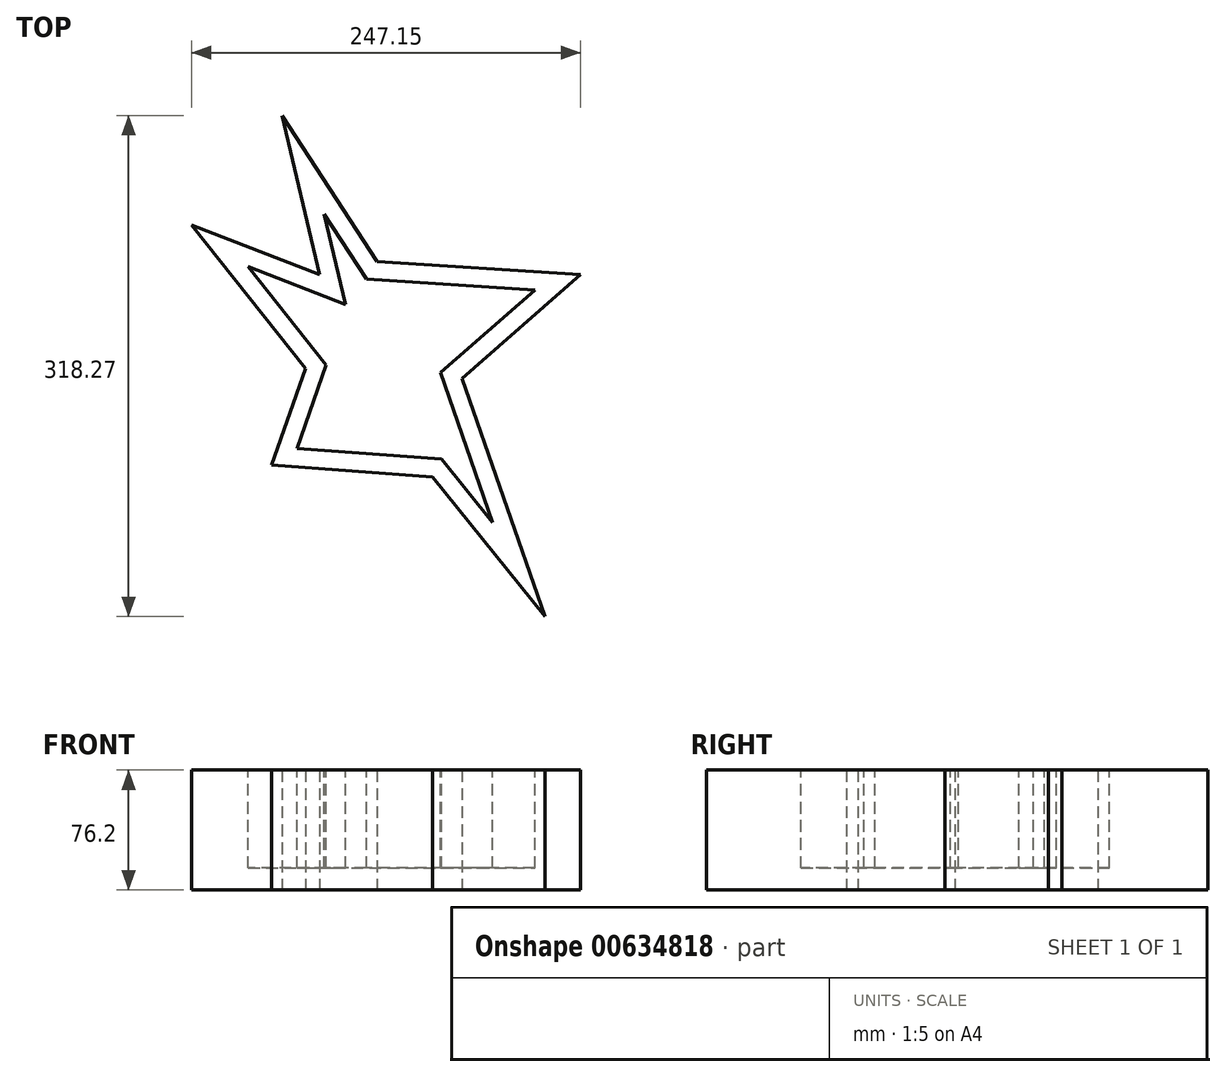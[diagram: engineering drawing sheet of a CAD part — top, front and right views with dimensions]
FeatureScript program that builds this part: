
annotation { "Feature Type Name" : "Feature", "Feature Type Description" : "" }
export const myFeature = defineFeature(function(context is Context, id is Id, definition is map)
    precondition{}
    {
        {
            var Q0;
            Q0=qCreatedBy(makeId("Top.planeOp"),FACE);
            var sketch = newSketch(context, id + "F0", { "sketchPlane" : qUnion([Q0])});
            skLineSegment(sketch, "E0", {"start": v(-35.22, 53.31) * mm, "end": v(-95.5, 145.95) * mm});
            skLineSegment(sketch, "E1", {"start": v(-95.5, 145.95) * mm, "end": v(-71.6, 44.85) * mm});
            skLineSegment(sketch, "E2", {"start": v(-71.6, 44.85) * mm, "end": v(-152.92, 76.24) * mm});
            skLineSegment(sketch, "E3", {"start": v(-152.92, 76.24) * mm, "end": v(-80.59, -14.67) * mm});
            skLineSegment(sketch, "E4", {"start": v(-80.59, -14.67) * mm, "end": v(-102.02, -76.14) * mm});
            skLineSegment(sketch, "E5", {"start": v(-102.02, -76.14) * mm, "end": v(0, -83.67) * mm});
            skLineSegment(sketch, "E6", {"start": v(0, -83.67) * mm, "end": v(71.54, -172.32) * mm});
            skLineSegment(sketch, "E7", {"start": v(71.54, -172.32) * mm, "end": v(18.7, -21.07) * mm});
            skLineSegment(sketch, "E8", {"start": v(18.7, -21.07) * mm, "end": v(94.23, 44.85) * mm});
            skLineSegment(sketch, "E9", {"start": v(94.23, 44.85) * mm, "end": v(-35.22, 53.31) * mm});
            skSolve(sketch);
        }
        {
            var Q0;
            Q0=makeQuery(id+"F0.imprint","IMPRINT",FACE,{"disambiguationData":[TD([[makeQuery(id+"F0.imprint","IMPRINT",EDGE,{"derivedFrom":sQuery(id+"F0.wireOp",EDGE,"E0")}),1.0]])]});
            extrude(context, id + "F1", {"entities" : qUnion([Q0]), "depth" : 76.2 * mm, "offsetDistance" : 25.4 * mm});
        }
        {
            var Q0;
            Q0=makeQuery(id+"F1.opExtrude","CAP_FACE",FACE,{"disambiguationData":[OSD([sQuery(id+"F0.wireOp",EDGE,"E0"),sQuery(id+"F0.wireOp",EDGE,"E1"),sQuery(id+"F0.wireOp",EDGE,"E2"),sQuery(id+"F0.wireOp",EDGE,"E3"),sQuery(id+"F0.wireOp",EDGE,"E4"),sQuery(id+"F0.wireOp",EDGE,"E5"),sQuery(id+"F0.wireOp",EDGE,"E6"),sQuery(id+"F0.wireOp",EDGE,"E7"),sQuery(id+"F0.wireOp",EDGE,"E8"),sQuery(id+"F0.wireOp",EDGE,"E9")])],"isStart":false});
            var sketch = newSketch(context, id + "F2", { "sketchPlane" : qUnion([Q0])});
            skLineSegment(sketch, "E10.0", {"start": v(38.25, -112.47) * mm, "end": v(5.06, -17.46) * mm});
            skLineSegment(sketch, "E10.1", {"start": v(5.91, -72.4) * mm, "end": v(38.25, -112.47) * mm});
            skLineSegment(sketch, "E10.2", {"start": v(5.06, -17.46) * mm, "end": v(65.21, 35.03) * mm});
            skLineSegment(sketch, "E10.3", {"start": v(-85.98, -65.6) * mm, "end": v(5.91, -72.4) * mm});
            skLineSegment(sketch, "E10.4", {"start": v(-67.43, -12.43) * mm, "end": v(-85.98, -65.6) * mm});
            skLineSegment(sketch, "E10.5", {"start": v(-116.98, 49.84) * mm, "end": v(-67.43, -12.43) * mm});
            skLineSegment(sketch, "E10.6", {"start": v(65.21, 35.03) * mm, "end": v(-41.82, 42.03) * mm});
            skLineSegment(sketch, "E10.7", {"start": v(-41.82, 42.03) * mm, "end": v(-68.68, 83.32) * mm});
            skLineSegment(sketch, "E10.8", {"start": v(-68.68, 83.32) * mm, "end": v(-55.12, 25.96) * mm});
            skLineSegment(sketch, "E10.9", {"start": v(-55.12, 25.96) * mm, "end": v(-116.98, 49.84) * mm});
            skSolve(sketch);
        }
        {
            var Q0;
            Q0=makeQuery(id+"F2.imprint","IMPRINT",FACE,{"disambiguationData":[TD([[makeQuery(id+"F2.imprint","IMPRINT",EDGE,{"derivedFrom":sQuery(id+"F2.wireOp",EDGE,"E10.0")}),1.0]])]});
            extrude(context, id + "F3", {"entities" : qUnion([Q0]), "operationType" : NewBodyOperationType.REMOVE, "oppositeDirection" : true, "depth" : 62.23 * mm, "offsetDistance" : 25.4 * mm});
        }
    });
